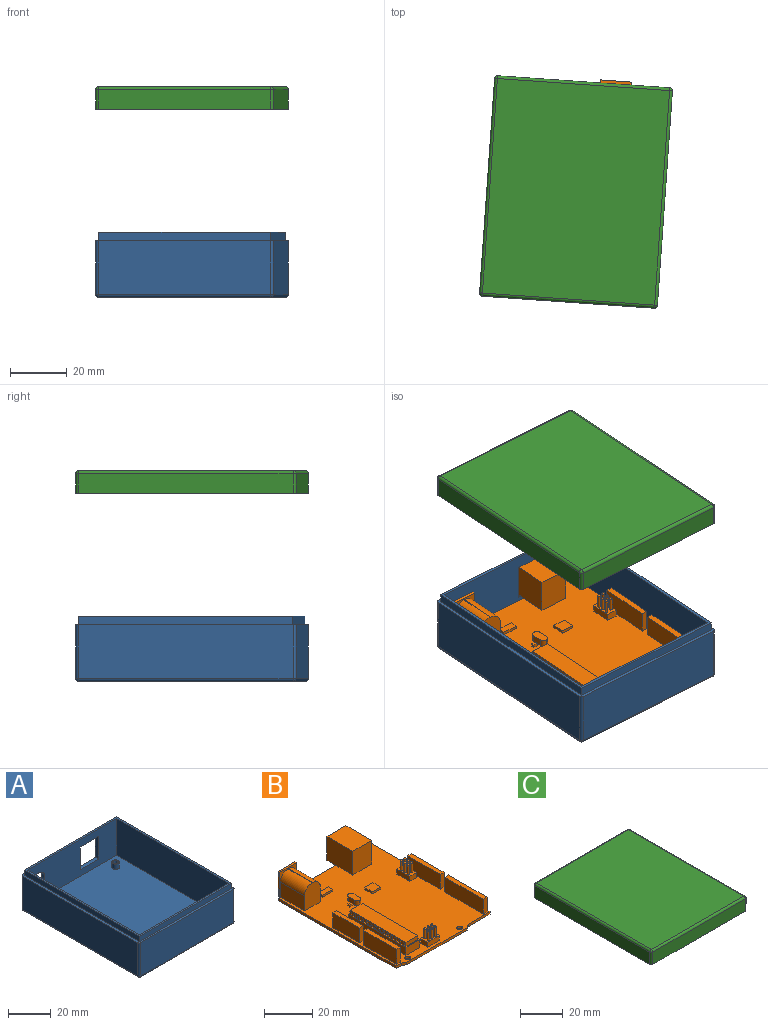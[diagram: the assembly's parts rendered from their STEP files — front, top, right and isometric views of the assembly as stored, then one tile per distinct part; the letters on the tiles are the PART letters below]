
ASSEMBLY  parts=3 mates=4
PART A: 49 faces, bbox 63x78x23 mm
  f0: plane 78x63mm, normal (0,0,1), area 294.3mm2, adj f2,f3,f4,f5,f32,f33,f34,f35
  f1: plane 59x21mm, normal (0,-1,0), area 1031.5mm2, adj f8,f9,f10,f27,f28,f29,f30,f31
  f2: plane 76x19mm, normal (1,0,0), area 1444mm2, adj f0,f39,f45,f48
  f3: plane 61x19mm, normal (0,-1,0), area 1159mm2, adj f0,f42,f46,f48
  f4: plane 76x19mm, normal (-1,0,0), area 1444mm2, adj f0,f37,f41,f42
  f5: plane 61x19mm, normal (0,1,0), area 951.5mm2, adj f0,f27,f28,f29,f30,f31,f37,f39
  f6: plane 76x61mm, normal (0,0,-1), area 4636mm2, adj f40,f41,f45,f46
  f7: plane 59x21mm, normal (0,1,0), area 1239mm2, adj f8,f9,f10,f36
  f8: plane 74x21mm, normal (-1,0,0), area 1554mm2, adj f1,f7,f10,f36
  f9: plane 74x21mm, normal (1,0,0), area 1554mm2, adj f1,f7,f10,f36
  f10: plane 74x59mm, normal (0,0,1), area 4327.5mm2, adj f1,f7,f8,f9,f12,f16,f20,f24
  f11: cylinder r=1.25mm len=3mm, axis (0,0,-1), area 23.6mm2, adj f13,f14
  f12: cylinder r=1.75mm len=3.5mm, axis (0,0,-1), area 33mm2, adj f10,f13
  f13: plane 3.5x3.5mm, normal (0,0,1), area 4.7mm2, adj f11,f12
  f14: plane 2.5x2.5mm, normal (0,0,1), area 4.9mm2, adj f11
  f15: cylinder r=1.25mm len=3mm, axis (0,0,-1), area 23.6mm2, adj f17,f18
  f16: cylinder r=1.75mm len=3.5mm, axis (0,0,-1), area 33mm2, adj f10,f17
  f17: plane 3.5x3.5mm, normal (0,0,1), area 4.7mm2, adj f15,f16
  f18: plane 2.5x2.5mm, normal (0,0,1), area 4.9mm2, adj f15
  f19: cylinder r=1.25mm len=3mm, axis (0,0,-1), area 23.6mm2, adj f21,f22
  f20: cylinder r=1.75mm len=3.5mm, axis (0,0,-1), area 33mm2, adj f10,f21
  f21: plane 3.5x3.5mm, normal (0,0,1), area 4.7mm2, adj f19,f20
  f22: plane 2.5x2.5mm, normal (0,0,1), area 4.9mm2, adj f19
  f23: cylinder r=1.25mm len=3mm, axis (0,0,-1), area 23.6mm2, adj f25,f26
  f24: cylinder r=1.75mm len=3.5mm, axis (0,0,-1), area 33mm2, adj f10,f25
  f25: plane 3.5x3.5mm, normal (0,0,1), area 4.7mm2, adj f23,f24
  f26: plane 2.5x2.5mm, normal (0,0,1), area 4.9mm2, adj f23
  f27: plane 13x2mm, normal (-1,0,0), area 26mm2, adj f1,f5,f28,f30
  f28: plane 12.11x2mm, normal (0,0,1), area 24.2mm2, adj f1,f5,f27,f29
  f29: plane 13x2mm, normal (1,0,0), area 26mm2, adj f1,f5,f28,f30
  f30: plane 12.11x2mm, normal (0,0,-1), area 24.2mm2, adj f1,f5,f27,f29
  f31: cylinder r=3.99mm len=7.98mm, axis (0,1,0), area 50.2mm2, adj f1,f5
  f32: plane 75.88x3mm, normal (1,0,0), area 227.6mm2, adj f0,f33,f35,f36
  f33: plane 60.88x3mm, normal (0,1,0), area 182.6mm2, adj f0,f32,f34,f36
  f34: plane 75.88x3mm, normal (-1,0,0), area 227.6mm2, adj f0,f33,f35,f36
  f35: plane 60.88x3mm, normal (0,-1,0), area 182.6mm2, adj f0,f32,f34,f36
  f36: plane 75.88x60.88mm, normal (0,0,1), area 252.9mm2, adj f1,f7,f8,f9,f32,f33,f34,f35
  f37: cylinder r=1mm len=19mm, axis (0,0,1), area 29.8mm2, adj f0,f4,f5,f38
  f38: sphere r=1mm, area 1.6mm2, adj f37,f40,f41
  f39: cylinder r=1mm len=19mm, axis (0,0,-1), area 29.8mm2, adj f0,f2,f5,f43
  f40: cylinder r=1mm len=61mm, axis (-1,0,0), area 95.8mm2, adj f5,f6,f38,f43
  f41: cylinder r=1mm len=76mm, axis (0,-1,0), area 119.4mm2, adj f4,f6,f38,f44
  f42: cylinder r=1mm len=19mm, axis (0,0,-1), area 29.8mm2, adj f0,f3,f4,f44
  f43: sphere r=1mm, area 1.6mm2, adj f39,f40,f45
  f44: sphere r=1mm, area 1.6mm2, adj f41,f42,f46
  f45: cylinder r=1mm len=76mm, axis (0,1,0), area 119.4mm2, adj f2,f6,f43,f47
  f46: cylinder r=1mm len=61mm, axis (1,0,0), area 95.8mm2, adj f3,f6,f44,f47
  f47: sphere r=1mm, area 1.6mm2, adj f45,f46,f48
  f48: cylinder r=1mm len=19mm, axis (0,0,1), area 29.8mm2, adj f0,f2,f3,f47
PART B: 244 faces, bbox 55x75.2x13.8 mm
  f0: plane 7x4mm, normal (0,0,1), area 23.3mm2, adj f194,f195,f196,f197,f226,f227,f228,f229
  f1: plane 7.5x4mm, normal (0,0,1), area 25.3mm2, adj f190,f191,f192,f193,f220,f221,f222,f223
  f2: plane 70x55mm, normal (0,0,1), area 3025.5mm2, adj f49,f50,f51,f52,f54,f55,f56,f57
  f3: plane 8.98x8.63mm, normal (0,1,0), area 52mm2, adj f179,f180,f181,f182,f183,f184,f185,f186
  f4: plane 1.5x0.4mm, normal (0,1,0), area 0.6mm2, adj f6,f46,f48,f178
  f5: plane 1.5x0.4mm, normal (0,-1,0), area 0.6mm2, adj f6,f46,f48,f178
  f6: plane 0.75x0.4mm, normal (0,0,1), area 0.3mm2, adj f4,f5,f46,f178
  f7: plane 1.5x0.4mm, normal (0,1,0), area 0.6mm2, adj f9,f46,f48,f177
  f8: plane 1.5x0.4mm, normal (0,-1,0), area 0.6mm2, adj f9,f46,f48,f177
  f9: plane 0.75x0.4mm, normal (0,0,1), area 0.3mm2, adj f7,f8,f46,f177
  f10: plane 1.5x0.4mm, normal (0,1,0), area 0.6mm2, adj f12,f46,f48,f176
  f11: plane 1.5x0.4mm, normal (0,-1,0), area 0.6mm2, adj f12,f46,f48,f176
  f12: plane 0.75x0.4mm, normal (0,0,1), area 0.3mm2, adj f10,f11,f46,f176
  f13: plane 1.5x0.4mm, normal (0,1,0), area 0.6mm2, adj f15,f46,f48,f175
  f14: plane 1.5x0.4mm, normal (0,-1,0), area 0.6mm2, adj f15,f46,f48,f175
  f15: plane 0.75x0.4mm, normal (0,0,1), area 0.3mm2, adj f13,f14,f46,f175
  f16: plane 1.5x0.4mm, normal (0,1,0), area 0.6mm2, adj f18,f46,f48,f174
  f17: plane 1.5x0.4mm, normal (0,-1,0), area 0.6mm2, adj f18,f46,f48,f174
  f18: plane 0.75x0.4mm, normal (0,0,1), area 0.3mm2, adj f16,f17,f46,f174
  f19: plane 1.5x0.4mm, normal (0,1,0), area 0.6mm2, adj f21,f46,f48,f173
  f20: plane 1.5x0.4mm, normal (0,-1,0), area 0.6mm2, adj f21,f46,f48,f173
  f21: plane 0.75x0.4mm, normal (0,0,1), area 0.3mm2, adj f19,f20,f46,f173
  f22: plane 1.5x0.4mm, normal (0,1,0), area 0.6mm2, adj f24,f46,f48,f172
  f23: plane 1.5x0.4mm, normal (0,-1,0), area 0.6mm2, adj f24,f46,f48,f172
  f24: plane 0.75x0.4mm, normal (0,0,1), area 0.3mm2, adj f22,f23,f46,f172
  f25: plane 1.5x0.4mm, normal (0,1,0), area 0.6mm2, adj f27,f46,f48,f171
  f26: plane 1.5x0.4mm, normal (0,-1,0), area 0.6mm2, adj f27,f46,f48,f171
  f27: plane 0.75x0.4mm, normal (0,0,1), area 0.3mm2, adj f25,f26,f46,f171
  f28: plane 1.5x0.4mm, normal (0,1,0), area 0.6mm2, adj f30,f46,f48,f170
  f29: plane 1.5x0.4mm, normal (0,-1,0), area 0.6mm2, adj f30,f46,f48,f170
  f30: plane 0.75x0.4mm, normal (0,0,1), area 0.3mm2, adj f28,f29,f46,f170
  f31: plane 1.5x0.4mm, normal (0,1,0), area 0.6mm2, adj f33,f46,f48,f169
  f32: plane 1.5x0.4mm, normal (0,-1,0), area 0.6mm2, adj f33,f46,f48,f169
  f33: plane 0.75x0.4mm, normal (0,0,1), area 0.3mm2, adj f31,f32,f46,f169
  f34: plane 1.5x0.4mm, normal (0,1,0), area 0.6mm2, adj f36,f46,f48,f168
  f35: plane 1.5x0.4mm, normal (0,-1,0), area 0.6mm2, adj f36,f46,f48,f168
  f36: plane 0.75x0.4mm, normal (0,0,1), area 0.3mm2, adj f34,f35,f46,f168
  f37: plane 1.5x0.4mm, normal (0,1,0), area 0.6mm2, adj f39,f46,f48,f167
  f38: plane 1.5x0.4mm, normal (0,-1,0), area 0.6mm2, adj f39,f46,f48,f167
  f39: plane 0.75x0.4mm, normal (0,0,1), area 0.3mm2, adj f37,f38,f46,f167
  f40: plane 1.5x0.4mm, normal (0,1,0), area 0.6mm2, adj f42,f46,f48,f166
  f41: plane 1.5x0.4mm, normal (0,-1,0), area 0.6mm2, adj f42,f46,f48,f166
  f42: plane 0.75x0.4mm, normal (0,0,1), area 0.3mm2, adj f40,f41,f46,f166
  f43: plane 1.5x0.4mm, normal (0,1,0), area 0.6mm2, adj f45,f46,f48,f165
  f44: plane 1.5x0.4mm, normal (0,-1,0), area 0.6mm2, adj f45,f46,f48,f165
  f45: plane 0.75x0.4mm, normal (0,0,1), area 0.3mm2, adj f43,f44,f46,f165
  f46: plane 32.63x2mm, normal (1,0,0), area 49.5mm2, adj f4,f5,f6,f7,f8,f9,f10,f11
  f47: plane 32.63x2mm, normal (-1,0,0), area 49.5mm2, adj f48,f106,f107,f108,f109,f110,f111,f112
  f48: plane 33.63x7.95mm, normal (0,0,1), area 32.2mm2, adj f4,f5,f7,f8,f10,f11,f13,f14
  f49: plane 33.63x4mm, normal (-1,0,0), area 134.5mm2, adj f2,f48,f50,f52
  f50: plane 7.95x4mm, normal (0,-1,0), area 31.8mm2, adj f2,f48,f49,f51
  f51: plane 33.63x4mm, normal (1,0,0), area 134.5mm2, adj f2,f48,f50,f52
  f52: plane 7.95x4mm, normal (0,1,0), area 31.8mm2, adj f2,f48,f49,f51
  f53: plane 6.98x6.98mm, normal (0,1,0), area 37.5mm2, adj f103,f104
  f54: plane 68.67x1.25mm, normal (1,0,0), area 85.8mm2, adj f2,f55,f58,f95
  f55: plane 55x1.25mm, normal (0,1,0), area 68.8mm2, adj f2,f54,f56,f58,f79,f84
  f56: plane 68.67x1.25mm, normal (-1,0,0), area 85.8mm2, adj f2,f55,f58,f92
  f57: plane 35.3x1.25mm, normal (0,-1,0), area 44.1mm2, adj f2,f58,f93,f94
  f58: plane 70x55mm, normal (0,0,-1), area 3816.6mm2, adj f54,f55,f56,f57,f92,f93,f94,f95
  f59: plane 7.5x2.22mm, normal (0,-1,0), area 16.7mm2, adj f2,f60,f62,f63
  f60: plane 22.58x7.5mm, normal (1,0,0), area 169.3mm2, adj f2,f59,f61,f63
  f61: plane 7.5x2.22mm, normal (0,1,0), area 16.7mm2, adj f2,f60,f62,f63
  f62: plane 22.58x7.5mm, normal (-1,0,0), area 169.3mm2, adj f2,f59,f61,f63
  f63: plane 22.58x2.22mm, normal (0,0,1), area 50.1mm2, adj f59,f60,f61,f62
  f64: plane 19.27x7.5mm, normal (-1,0,0), area 144.5mm2, adj f2,f65,f67,f68
  f65: plane 7.5x2.22mm, normal (0,-1,0), area 16.7mm2, adj f2,f64,f66,f68
  f66: plane 19.27x7.5mm, normal (1,0,0), area 144.5mm2, adj f2,f65,f67,f68
  f67: plane 7.5x2.22mm, normal (0,1,0), area 16.7mm2, adj f2,f64,f66,f68
  f68: plane 19.27x2.22mm, normal (0,0,1), area 42.8mm2, adj f64,f65,f66,f67
  f69: plane 19.1x7.5mm, normal (-1,0,0), area 143.2mm2, adj f2,f70,f72,f73
  f70: plane 7.5x2.22mm, normal (0,-1,0), area 16.7mm2, adj f2,f69,f71,f73
  f71: plane 19.1x7.5mm, normal (1,0,0), area 143.2mm2, adj f2,f70,f72,f73
  f72: plane 7.5x2.22mm, normal (0,1,0), area 16.7mm2, adj f2,f69,f71,f73
  f73: plane 19.1x2.22mm, normal (0,0,1), area 42.4mm2, adj f69,f70,f71,f72
  f74: plane 15.53x7.5mm, normal (1,0,0), area 116.5mm2, adj f2,f75,f77,f78
  f75: plane 7.5x2.22mm, normal (0,1,0), area 16.7mm2, adj f2,f74,f76,f78
  f76: plane 15.53x7.5mm, normal (-1,0,0), area 116.5mm2, adj f2,f75,f77,f78
  f77: plane 7.5x2.22mm, normal (0,-1,0), area 16.7mm2, adj f2,f74,f76,f78
  f78: plane 15.53x2.22mm, normal (0,0,1), area 34.5mm2, adj f74,f75,f76,f77
  f79: plane 9.89x1.2mm, normal (0,0,-1), area 11.7mm2, adj f55,f80,f82,f98,f99,f101,f102
  f80: plane 14.15x7.5mm, normal (-1,0,0), area 106.1mm2, adj f2,f79,f81,f90,f98
  f81: plane 12x9.24mm, normal (0,-1,0), area 102.2mm2, adj f2,f80,f82,f83,f90,f91
  f82: plane 14.15x7.5mm, normal (1,0,0), area 106.1mm2, adj f2,f79,f81,f91,f98
  f83: plane 14.15x0.24mm, normal (0,0,1), area 3.4mm2, adj f81,f90,f91,f98
  f84: plane 11.11x5.16mm, normal (0,0,-1), area 57.3mm2, adj f55,f85,f87,f88
  f85: plane 15.05x12mm, normal (-1,0,0), area 180.6mm2, adj f2,f84,f86,f88,f89
  f86: plane 12x11.11mm, normal (0,-1,0), area 133.3mm2, adj f2,f85,f87,f89
  f87: plane 15.05x12mm, normal (1,0,0), area 180.6mm2, adj f2,f84,f86,f88,f89
  f88: plane 12x11.11mm, normal (0,1,0), area 60.1mm2, adj f84,f85,f87,f89,f179,f180,f181,f182
  f89: plane 15.05x11.11mm, normal (0,0,1), area 167.2mm2, adj f85,f86,f87,f88
  f90: cylinder r=4.5mm len=14.15mm, axis (0,1,0), area 100mm2, adj f80,f81,f83,f98
  f91: cylinder r=4.5mm len=14.15mm, axis (0,-1,0), area 100mm2, adj f81,f82,f83,f98
  f92: plane 2.98x1.25mm, normal (0,-1,0), area 3.7mm2, adj f2,f56,f58,f93
  f93: plane 2.01x1.33mm, normal (-0.55,-0.83,0), area 3mm2, adj f2,f57,f58,f92
  f94: plane 2.01x1.33mm, normal (0.55,-0.83,0), area 3mm2, adj f2,f57,f58,f95
  f95: plane 12.71x1.25mm, normal (0,-1,0), area 15.9mm2, adj f2,f54,f58,f94
  f96: cylinder r=1.25mm len=2.5mm, axis (0,0,1), area 9.8mm2, adj f2,f58
  f97: cylinder r=1.25mm len=2.5mm, axis (0,0,1), area 9.8mm2, adj f2,f58
  f98: plane 12.57x9.89mm, normal (0,-1,0), area 22.1mm2, adj f79,f80,f82,f83,f90,f91,f99,f100
  f99: plane 12.57x1mm, normal (-1,0,0), area 12.6mm2, adj f79,f98,f100,f102
  f100: plane 9.89x1mm, normal (0,0,1), area 9.9mm2, adj f98,f99,f101,f102
  f101: plane 12.57x1mm, normal (1,0,0), area 12.6mm2, adj f79,f98,f100,f102
  f102: plane 12.57x9.89mm, normal (0,1,0), area 86mm2, adj f79,f99,f100,f101,f103
  f103: cylinder r=3.49mm len=12mm, axis (0,1,0), area 263.3mm2, adj f53,f102
  f104: cylinder r=0.5mm len=8mm, axis (0,-1,0), area 25.1mm2, adj f53,f105
  f105: plane 1x1mm, normal (0,1,0), area 0.8mm2, adj f104
  f106: plane 6.95x2mm, normal (0,1,0), area 13.9mm2, adj f46,f47,f48,f108
  f107: plane 6.95x2mm, normal (0,-1,0), area 13.9mm2, adj f46,f47,f48,f108
  f108: plane 32.63x6.95mm, normal (0,0,1), area 226.7mm2, adj f46,f47,f106,f107
  f109: plane 1.5x0.4mm, normal (0,1,0), area 0.6mm2, adj f47,f48,f111,f164
  f110: plane 1.5x0.4mm, normal (0,-1,0), area 0.6mm2, adj f47,f48,f111,f164
  f111: plane 0.75x0.4mm, normal (0,0,1), area 0.3mm2, adj f47,f109,f110,f164
  f112: plane 1.5x0.4mm, normal (0,1,0), area 0.6mm2, adj f47,f48,f114,f163
  f113: plane 1.5x0.4mm, normal (0,-1,0), area 0.6mm2, adj f47,f48,f114,f163
  f114: plane 0.75x0.4mm, normal (0,0,1), area 0.3mm2, adj f47,f112,f113,f163
  f115: plane 1.5x0.4mm, normal (0,1,0), area 0.6mm2, adj f47,f48,f117,f162
  f116: plane 1.5x0.4mm, normal (0,-1,0), area 0.6mm2, adj f47,f48,f117,f162
  f117: plane 0.75x0.4mm, normal (0,0,1), area 0.3mm2, adj f47,f115,f116,f162
  f118: plane 1.5x0.4mm, normal (0,1,0), area 0.6mm2, adj f47,f48,f120,f161
  f119: plane 1.5x0.4mm, normal (0,-1,0), area 0.6mm2, adj f47,f48,f120,f161
  f120: plane 0.75x0.4mm, normal (0,0,1), area 0.3mm2, adj f47,f118,f119,f161
  f121: plane 1.5x0.4mm, normal (0,1,0), area 0.6mm2, adj f47,f48,f123,f160
  f122: plane 1.5x0.4mm, normal (0,-1,0), area 0.6mm2, adj f47,f48,f123,f160
  f123: plane 0.75x0.4mm, normal (0,0,1), area 0.3mm2, adj f47,f121,f122,f160
  f124: plane 1.5x0.4mm, normal (0,1,0), area 0.6mm2, adj f47,f48,f126,f159
  f125: plane 1.5x0.4mm, normal (0,-1,0), area 0.6mm2, adj f47,f48,f126,f159
  f126: plane 0.75x0.4mm, normal (0,0,1), area 0.3mm2, adj f47,f124,f125,f159
  f127: plane 1.5x0.4mm, normal (0,1,0), area 0.6mm2, adj f47,f48,f129,f158
  f128: plane 1.5x0.4mm, normal (0,-1,0), area 0.6mm2, adj f47,f48,f129,f158
  f129: plane 0.75x0.4mm, normal (0,0,1), area 0.3mm2, adj f47,f127,f128,f158
  f130: plane 1.5x0.4mm, normal (0,1,0), area 0.6mm2, adj f47,f48,f132,f157
  f131: plane 1.5x0.4mm, normal (0,-1,0), area 0.6mm2, adj f47,f48,f132,f157
  f132: plane 0.75x0.4mm, normal (0,0,1), area 0.3mm2, adj f47,f130,f131,f157
  f133: plane 1.5x0.4mm, normal (0,1,0), area 0.6mm2, adj f47,f48,f135,f156
  f134: plane 1.5x0.4mm, normal (0,-1,0), area 0.6mm2, adj f47,f48,f135,f156
  f135: plane 0.75x0.4mm, normal (0,0,1), area 0.3mm2, adj f47,f133,f134,f156
  f136: plane 1.5x0.4mm, normal (0,1,0), area 0.6mm2, adj f47,f48,f138,f155
  f137: plane 1.5x0.4mm, normal (0,-1,0), area 0.6mm2, adj f47,f48,f138,f155
  f138: plane 0.75x0.4mm, normal (0,0,1), area 0.3mm2, adj f47,f136,f137,f155
  f139: plane 1.5x0.4mm, normal (0,1,0), area 0.6mm2, adj f47,f48,f141,f154
  f140: plane 1.5x0.4mm, normal (0,-1,0), area 0.6mm2, adj f47,f48,f141,f154
  f141: plane 0.75x0.4mm, normal (0,0,1), area 0.3mm2, adj f47,f139,f140,f154
  f142: plane 1.5x0.4mm, normal (0,1,0), area 0.6mm2, adj f47,f48,f144,f153
  f143: plane 1.5x0.4mm, normal (0,-1,0), area 0.6mm2, adj f47,f48,f144,f153
  f144: plane 0.75x0.4mm, normal (0,0,1), area 0.3mm2, adj f47,f142,f143,f153
  f145: plane 1.5x0.4mm, normal (0,1,0), area 0.6mm2, adj f47,f48,f147,f152
  f146: plane 1.5x0.4mm, normal (0,-1,0), area 0.6mm2, adj f47,f48,f147,f152
  f147: plane 0.75x0.4mm, normal (0,0,1), area 0.3mm2, adj f47,f145,f146,f152
  f148: plane 1.5x0.4mm, normal (0,1,0), area 0.6mm2, adj f47,f48,f150,f151
  f149: plane 1.5x0.4mm, normal (0,-1,0), area 0.6mm2, adj f47,f48,f150,f151
  f150: plane 0.75x0.4mm, normal (0,0,1), area 0.3mm2, adj f47,f148,f149,f151
  f151: plane 1.5x0.75mm, normal (-1,0,0), area 1.1mm2, adj f48,f148,f149,f150
  f152: plane 1.5x0.75mm, normal (-1,0,0), area 1.1mm2, adj f48,f145,f146,f147
  f153: plane 1.5x0.75mm, normal (-1,0,0), area 1.1mm2, adj f48,f142,f143,f144
  f154: plane 1.5x0.75mm, normal (-1,0,0), area 1.1mm2, adj f48,f139,f140,f141
  f155: plane 1.5x0.75mm, normal (-1,0,0), area 1.1mm2, adj f48,f136,f137,f138
  f156: plane 1.5x0.75mm, normal (-1,0,0), area 1.1mm2, adj f48,f133,f134,f135
  f157: plane 1.5x0.75mm, normal (-1,0,0), area 1.1mm2, adj f48,f130,f131,f132
  f158: plane 1.5x0.75mm, normal (-1,0,0), area 1.1mm2, adj f48,f127,f128,f129
  f159: plane 1.5x0.75mm, normal (-1,0,0), area 1.1mm2, adj f48,f124,f125,f126
  f160: plane 1.5x0.75mm, normal (-1,0,0), area 1.1mm2, adj f48,f121,f122,f123
  f161: plane 1.5x0.75mm, normal (-1,0,0), area 1.1mm2, adj f48,f118,f119,f120
  f162: plane 1.5x0.75mm, normal (-1,0,0), area 1.1mm2, adj f48,f115,f116,f117
  f163: plane 1.5x0.75mm, normal (-1,0,0), area 1.1mm2, adj f48,f112,f113,f114
  f164: plane 1.5x0.75mm, normal (-1,0,0), area 1.1mm2, adj f48,f109,f110,f111
  f165: plane 1.5x0.75mm, normal (1,0,0), area 1.1mm2, adj f43,f44,f45,f48
  f166: plane 1.5x0.75mm, normal (1,0,0), area 1.1mm2, adj f40,f41,f42,f48
  f167: plane 1.5x0.75mm, normal (1,0,0), area 1.1mm2, adj f37,f38,f39,f48
  f168: plane 1.5x0.75mm, normal (1,0,0), area 1.1mm2, adj f34,f35,f36,f48
  f169: plane 1.5x0.75mm, normal (1,0,0), area 1.1mm2, adj f31,f32,f33,f48
  f170: plane 1.5x0.75mm, normal (1,0,0), area 1.1mm2, adj f28,f29,f30,f48
  f171: plane 1.5x0.75mm, normal (1,0,0), area 1.1mm2, adj f25,f26,f27,f48
  f172: plane 1.5x0.75mm, normal (1,0,0), area 1.1mm2, adj f22,f23,f24,f48
  f173: plane 1.5x0.75mm, normal (1,0,0), area 1.1mm2, adj f19,f20,f21,f48
  f174: plane 1.5x0.75mm, normal (1,0,0), area 1.1mm2, adj f16,f17,f18,f48
  f175: plane 1.5x0.75mm, normal (1,0,0), area 1.1mm2, adj f13,f14,f15,f48
  f176: plane 1.5x0.75mm, normal (1,0,0), area 1.1mm2, adj f10,f11,f12,f48
  f177: plane 1.5x0.75mm, normal (1,0,0), area 1.1mm2, adj f7,f8,f9,f48
  f178: plane 1.5x0.75mm, normal (1,0,0), area 1.1mm2, adj f4,f5,f6,f48
  f179: plane 10x6.73mm, normal (1,0,0), area 67.3mm2, adj f3,f88,f180,f184
  f180: plane 10x8.63mm, normal (0,0,1), area 86.3mm2, adj f3,f88,f179,f181
  f181: plane 10x6.73mm, normal (-1,0,0), area 67.3mm2, adj f3,f88,f180,f182
  f182: plane 10x2.24mm, normal (-0.76,0,-0.65), area 29.4mm2, adj f3,f88,f181,f183
  f183: plane 10x4.83mm, normal (0,0,-1), area 48.3mm2, adj f3,f88,f182,f184
  f184: plane 10x2.24mm, normal (0.76,0,-0.65), area 29.4mm2, adj f3,f88,f179,f183
  f185: plane 8x3.45mm, normal (-1,0,0), area 27.6mm2, adj f3,f186,f188,f189
  f186: plane 8x6.13mm, normal (0,0,1), area 49mm2, adj f3,f185,f187,f189
  f187: plane 8x3.45mm, normal (1,0,0), area 27.6mm2, adj f3,f186,f188,f189
  f188: plane 8x6.13mm, normal (0,0,-1), area 49mm2, adj f3,f185,f187,f189
  f189: plane 6.13x3.45mm, normal (0,1,0), area 21.2mm2, adj f185,f186,f187,f188
  f190: plane 7.5x2.5mm, normal (-1,0,0), area 18.7mm2, adj f1,f2,f191,f193
  f191: plane 4x2.5mm, normal (0,-1,0), area 10mm2, adj f1,f2,f190,f192
  f192: plane 7.5x2.5mm, normal (1,0,0), area 18.7mm2, adj f1,f2,f191,f193
  f193: plane 4x2.5mm, normal (0,1,0), area 10mm2, adj f1,f2,f190,f192
  f194: plane 4x2.5mm, normal (-1,0,0), area 10mm2, adj f0,f2,f195,f197
  f195: plane 7x2.5mm, normal (0,-1,0), area 17.5mm2, adj f0,f2,f194,f196
  f196: plane 4x2.5mm, normal (1,0,0), area 10mm2, adj f0,f2,f195,f197
  f197: plane 7x2.5mm, normal (0,1,0), area 17.5mm2, adj f0,f2,f194,f196
  f198: plane 3.5x2.5mm, normal (-1,0,0), area 8.8mm2, adj f2,f200,f201,f203
  f199: plane 3.5x2.5mm, normal (1,0,0), area 8.8mm2, adj f2,f200,f202,f204
  f200: plane 6.5x3mm, normal (0,0,1), area 17.6mm2, adj f198,f199,f201,f202,f203,f204
  f201: cylinder r=1.5mm len=2.5mm, axis (0,0,-1), area 5.9mm2, adj f2,f198,f200,f202
  f202: cylinder r=1.5mm len=2.5mm, axis (0,0,-1), area 5.9mm2, adj f2,f199,f200,f201
  f203: cylinder r=1.5mm len=2.5mm, axis (0,0,-1), area 5.9mm2, adj f2,f198,f200,f204
  f204: cylinder r=1.5mm len=2.5mm, axis (0,0,-1), area 5.9mm2, adj f2,f199,f200,f203
  f205: plane 2.66x1mm, normal (-1,0,0), area 2.7mm2, adj f2,f206,f208,f209
  f206: plane 5.95x1mm, normal (0,-1,0), area 6mm2, adj f2,f205,f207,f209
  f207: plane 2.66x1mm, normal (1,0,0), area 2.7mm2, adj f2,f206,f208,f209
  f208: plane 5.95x1mm, normal (0,1,0), area 6mm2, adj f2,f205,f207,f209
  f209: plane 5.95x2.66mm, normal (0,0,1), area 15.9mm2, adj f205,f206,f207,f208
  f210: plane 1.1x1mm, normal (-1,0,0), area 1.1mm2, adj f2,f211,f213,f214
  f211: plane 1.57x1mm, normal (0,-1,0), area 1.6mm2, adj f2,f210,f212,f214
  f212: plane 1.1x1mm, normal (1,0,0), area 1.1mm2, adj f2,f211,f213,f214
  f213: plane 1.57x1mm, normal (0,1,0), area 1.6mm2, adj f2,f210,f212,f214
  f214: plane 1.57x1.1mm, normal (0,0,1), area 1.7mm2, adj f210,f211,f212,f213
  f215: plane 4.54x1mm, normal (-1,0,0), area 4.5mm2, adj f2,f216,f218,f219
  f216: plane 4.86x1mm, normal (0,-1,0), area 4.9mm2, adj f2,f215,f217,f219
  f217: plane 4.54x1mm, normal (1,0,0), area 4.5mm2, adj f2,f216,f218,f219
  f218: plane 4.86x1mm, normal (0,1,0), area 4.9mm2, adj f2,f215,f217,f219
  f219: plane 4.86x4.54mm, normal (0,0,1), area 22.1mm2, adj f215,f216,f217,f218
  f220: cylinder r=0.5mm len=4.5mm, axis (0,0,-1), area 14.1mm2, adj f1,f237
  f221: cylinder r=0.5mm len=4.5mm, axis (0,0,-1), area 14.1mm2, adj f1,f238
  f222: cylinder r=0.5mm len=4.5mm, axis (0,0,-1), area 14.1mm2, adj f1,f235
  f223: cylinder r=0.5mm len=4.5mm, axis (0,0,-1), area 14.1mm2, adj f1,f232
  f224: cylinder r=0.5mm len=4.5mm, axis (0,0,-1), area 14.1mm2, adj f1,f233
  f225: cylinder r=0.5mm len=4.5mm, axis (0,0,-1), area 14.1mm2, adj f1,f234
  f226: cylinder r=0.5mm len=4.5mm, axis (0,0,-1), area 14.1mm2, adj f0,f239
  f227: cylinder r=0.5mm len=4.5mm, axis (0,0,-1), area 14.1mm2, adj f0,f236
  f228: cylinder r=0.5mm len=4.5mm, axis (0,0,-1), area 14.1mm2, adj f0,f242
  f229: cylinder r=0.5mm len=4.5mm, axis (0,0,-1), area 14.1mm2, adj f0,f241
  f230: cylinder r=0.5mm len=4.5mm, axis (0,0,-1), area 14.1mm2, adj f0,f240
  f231: cylinder r=0.5mm len=4.5mm, axis (0,0,-1), area 14.1mm2, adj f0,f243
  f232: sphere r=0.5mm, area 1.6mm2, adj f223
  f233: sphere r=0.5mm, area 1.6mm2, adj f224
  f234: sphere r=0.5mm, area 1.6mm2, adj f225
  f235: sphere r=0.5mm, area 1.6mm2, adj f222
  f236: sphere r=0.5mm, area 1.6mm2, adj f227
  f237: sphere r=0.5mm, area 1.6mm2, adj f220
  f238: sphere r=0.5mm, area 1.6mm2, adj f221
  f239: sphere r=0.5mm, area 1.6mm2, adj f226
  f240: sphere r=0.5mm, area 1.6mm2, adj f230
  f241: sphere r=0.5mm, area 1.6mm2, adj f229
  f242: sphere r=0.5mm, area 1.6mm2, adj f228
  f243: sphere r=0.5mm, area 1.6mm2, adj f231
PART C: 28 faces, bbox 63x78x8 mm
  f0: plane 78x63mm, normal (0,0,-1), area 294.3mm2, adj f1,f2,f3,f4,f6,f7,f8,f9
  f1: plane 76x7mm, normal (1,0,0), area 532mm2, adj f0,f18,f24,f27
  f2: plane 61x7mm, normal (0,1,0), area 427mm2, adj f0,f21,f25,f27
  f3: plane 76x7mm, normal (-1,0,0), area 532mm2, adj f0,f16,f20,f21
  f4: plane 61x7mm, normal (0,-1,0), area 427mm2, adj f0,f16,f18,f19
  f5: plane 76x61mm, normal (0,0,1), area 4636mm2, adj f19,f20,f24,f25
  f6: plane 75.88x3mm, normal (-1,0,0), area 227.6mm2, adj f0,f7,f9,f10
  f7: plane 60.88x3mm, normal (0,-1,0), area 182.6mm2, adj f0,f6,f8,f10
  f8: plane 75.88x3mm, normal (1,0,0), area 227.6mm2, adj f0,f7,f9,f10
  f9: plane 60.88x3mm, normal (0,1,0), area 182.6mm2, adj f0,f6,f8,f10
  f10: plane 75.88x60.88mm, normal (0,0,-1), area 252.9mm2, adj f6,f7,f8,f9,f12,f13,f14,f15
  f11: plane 74x59mm, normal (0,0,-1), area 4366mm2, adj f12,f13,f14,f15
  f12: plane 74x3mm, normal (1,0,0), area 222mm2, adj f10,f11,f13,f15
  f13: plane 59x3mm, normal (0,-1,0), area 177mm2, adj f10,f11,f12,f14
  f14: plane 74x3mm, normal (-1,0,0), area 222mm2, adj f10,f11,f13,f15
  f15: plane 59x3mm, normal (0,1,0), area 177mm2, adj f10,f11,f12,f14
  f16: cylinder r=1mm len=7mm, axis (0,0,1), area 11mm2, adj f0,f3,f4,f17
  f17: sphere r=1mm, area 1.6mm2, adj f16,f19,f20
  f18: cylinder r=1mm len=7mm, axis (0,0,-1), area 11mm2, adj f0,f1,f4,f22
  f19: cylinder r=1mm len=61mm, axis (-1,0,0), area 95.8mm2, adj f4,f5,f17,f22
  f20: cylinder r=1mm len=76mm, axis (0,1,0), area 119.4mm2, adj f3,f5,f17,f23
  f21: cylinder r=1mm len=7mm, axis (0,0,-1), area 11mm2, adj f0,f2,f3,f23
  f22: sphere r=1mm, area 1.6mm2, adj f18,f19,f24
  f23: sphere r=1mm, area 1.6mm2, adj f20,f21,f25
  f24: cylinder r=1mm len=76mm, axis (0,-1,0), area 119.4mm2, adj f1,f5,f22,f26
  f25: cylinder r=1mm len=61mm, axis (1,0,0), area 95.8mm2, adj f2,f5,f23,f26
  f26: sphere r=1mm, area 1.6mm2, adj f24,f25,f27
  f27: cylinder r=1mm len=7mm, axis (0,0,1), area 11mm2, adj f0,f1,f2,f26
PLACE A rot(axis=(0,0,-1),4deg) t=(-40.8,-55.1,23.35)mm fixed
PLACE B rot(axis=(0,0,-1),4deg) t=(-40.8,-55.1,23.35)mm
PLACE C rot(axis=(0,0,-1),4deg) t=(-40.8,-55.1,69.77)mm
MATE planar C.f6 <-> A.f32  axis (-1,0.07,0) through (-10.41,-57.19,86.27)mm
MATE cylindrical A.f15 <-> B.f96  axis (0,0,1) through (-63.06,-86.62,23.35)mm
MATE planar C.f9 <-> A.f35  axis (0.07,1,0) through (-43.42,-92.91,86.27)mm
MATE planar B.f58 <-> A.f11  axis (0,0,-1) through (-40.84,-54.8,23.35)mm
